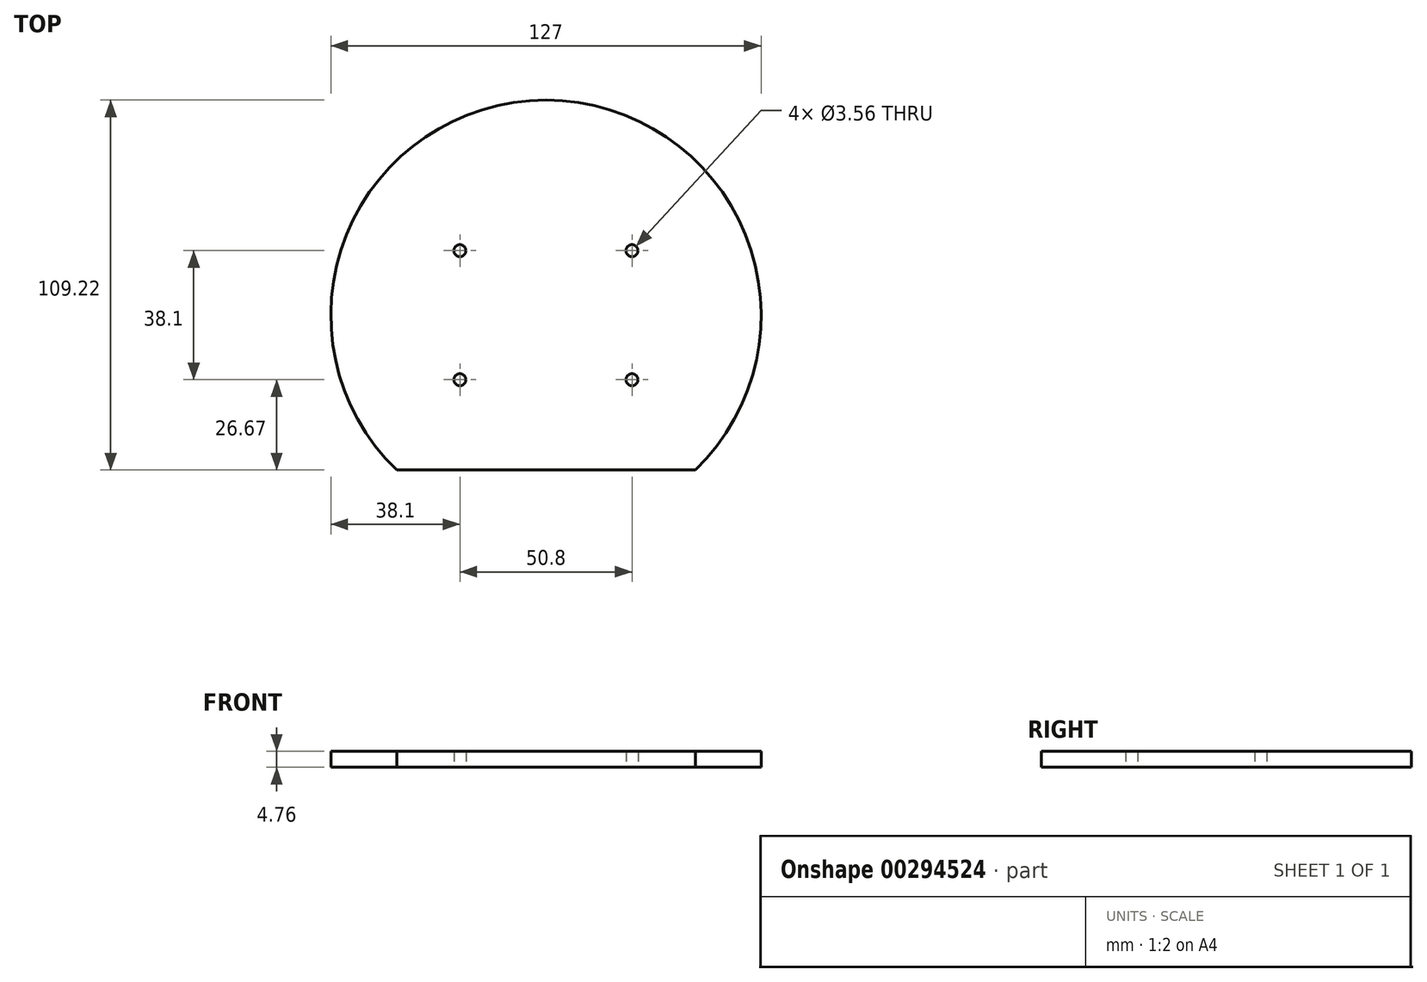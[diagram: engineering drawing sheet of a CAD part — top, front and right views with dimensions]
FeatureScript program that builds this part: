
annotation { "Feature Type Name" : "Feature", "Feature Type Description" : "" }
export const myFeature = defineFeature(function(context is Context, id is Id, definition is map)
    precondition{}
    {
        {
            var Q0;
            Q0=qCreatedBy(makeId("Top.planeOp"),FACE);
            var sketch = newSketch(context, id + "F0", { "sketchPlane" : qUnion([Q0])});
            skCircle(sketch, "E0", {"center": v(0, 0) * mm, "radius": 63.5 * mm});
            skLineSegment(sketch, "E1", {"start": v(0, 0) * mm, "end": v(63.5, 0) * mm, "construction": true});
            skLineSegment(sketch, "E2", {"start": v(25.4, 0) * mm, "end": v(25.4, 19.05) * mm, "construction": true});
            skCircle(sketch, "E3", {"center": v(25.4, 19.05) * mm, "radius": 1.78 * mm});
            skCircle(sketch, "E4.MirrorC", {"center": v(25.4, -19.05) * mm, "radius": 1.78 * mm});
            skLineSegment(sketch, "E5", {"start": v(0, 0) * mm, "end": v(0, -33.46) * mm, "construction": true});
            skCircle(sketch, "E6.MirrorC", {"center": v(-25.4, 19.05) * mm, "radius": 1.78 * mm});
            skCircle(sketch, "E7.MirrorC", {"center": v(-25.4, -19.05) * mm, "radius": 1.78 * mm});
            skSolve(sketch);
        }
        {
            var Q0;
            Q0=makeQuery(id+"F0.imprint","IMPRINT",FACE,{"disambiguationData":[TD([[makeQuery(id+"F0.imprint","IMPRINT",EDGE,{"derivedFrom":sQuery(id+"F0.wireOp",EDGE,"E0")}),1.0]])]});
            extrude(context, id + "F1", {"entities" : qUnion([Q0]), "depth" : 4.76 * mm});
        }
        {
            var Q0;
            Q0=makeQuery(id+"F1.opExtrude","CAP_FACE",FACE,{"disambiguationData":[OSD([sQuery(id+"F0.wireOp",EDGE,"E0"),sQuery(id+"F0.wireOp",EDGE,"E3"),sQuery(id+"F0.wireOp",EDGE,"E4.MirrorC"),sQuery(id+"F0.wireOp",EDGE,"E6.MirrorC"),sQuery(id+"F0.wireOp",EDGE,"E7.MirrorC")])],"isStart":false});
            var sketch = newSketch(context, id + "F2", { "sketchPlane" : qUnion([Q0])});
            skLineSegment(sketch, "E8", {"start": v(-44.07, -45.72) * mm, "end": v(44.07, -45.72) * mm});
            skLineSegment(sketch, "E9", {"start": v(0, 0) * mm, "end": v(0, 63.5) * mm});
            skSolve(sketch);
        }
        {
            var Q0;
            {var subQ0=sQuery(id+"F2.wireOp",EDGE,"E8");Q0=makeQuery(id+"F2.imprint","IMPRINT",FACE,{"disambiguationData":[TD([[makeQuery(id+"F2.imprint","IMPRINT",EDGE,{"derivedFrom":subQ0}),-1.0]])]});}
            extrude(context, id + "F3", {"entities" : qUnion([Q0]), "operationType" : NewBodyOperationType.REMOVE, "oppositeDirection" : true, "depth" : 25.4 * mm});
        }
    });
